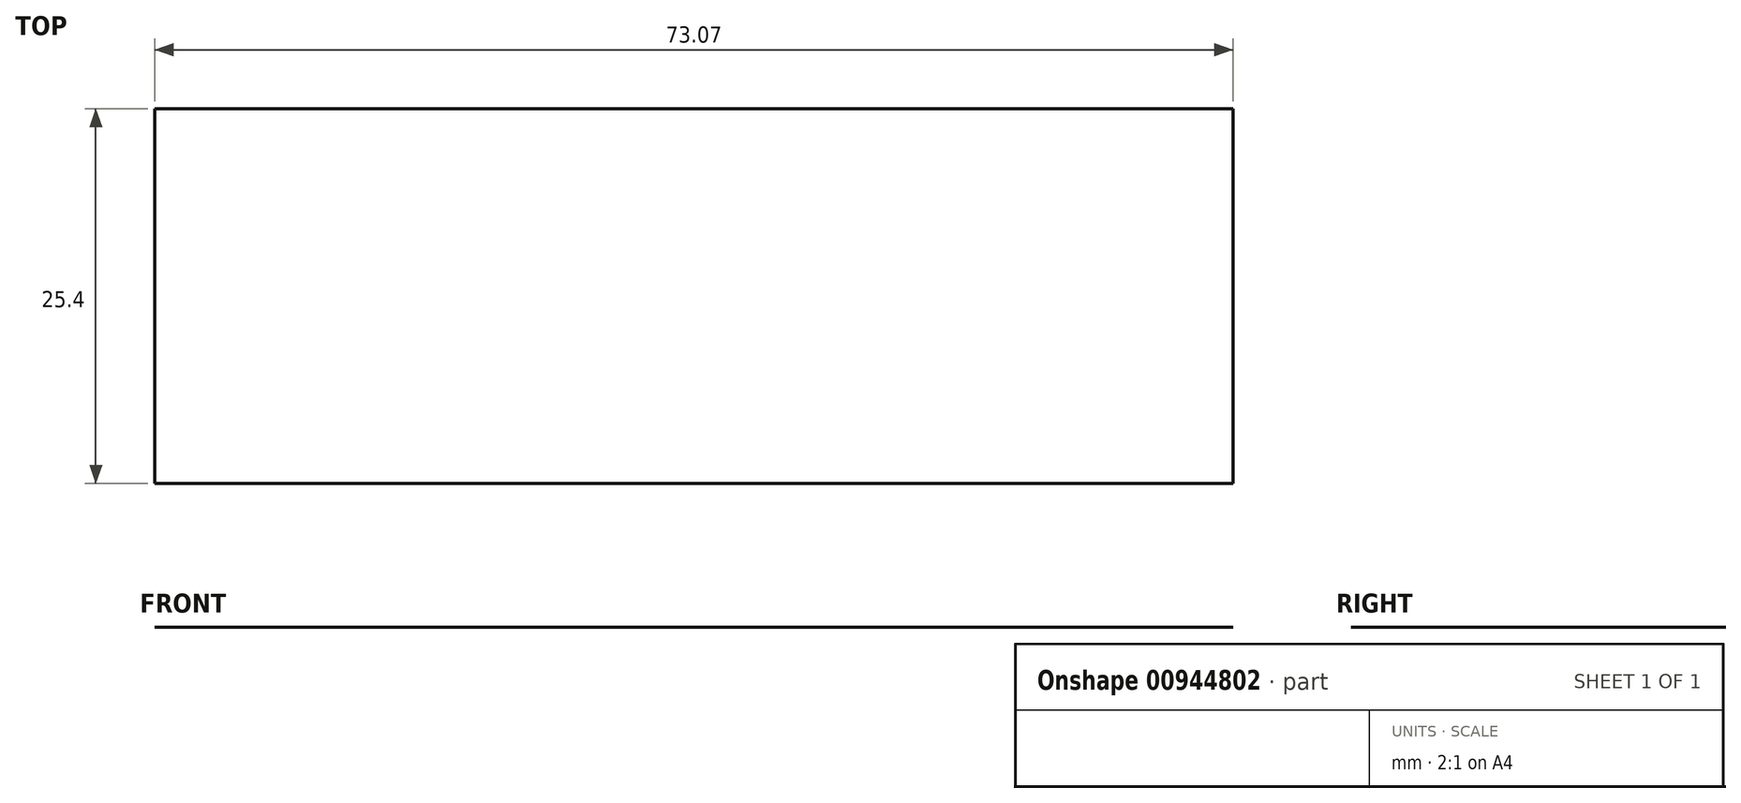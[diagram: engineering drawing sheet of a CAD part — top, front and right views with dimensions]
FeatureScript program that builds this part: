
annotation { "Feature Type Name" : "Feature", "Feature Type Description" : "" }
export const myFeature = defineFeature(function(context is Context, id is Id, definition is map)
    precondition{}
    {
        {
            var Q0;
            Q0=qCreatedBy(makeId("Front.planeOp"),FACE);
            var sketch = newSketch(context, id + "F0", { "sketchPlane" : qUnion([Q0])});
            skLineSegment(sketch, "E0.bottom", {"start": v(-34.39, 25.96) * mm, "end": v(38.68, 25.96) * mm});
            skLineSegment(sketch, "E0.top", {"start": v(-34.39, -37.55) * mm, "end": v(38.68, -37.55) * mm});
            skLineSegment(sketch, "E0.left", {"start": v(-34.39, 25.96) * mm, "end": v(-34.39, -37.55) * mm});
            skLineSegment(sketch, "E0.right", {"start": v(38.68, 25.96) * mm, "end": v(38.68, -37.55) * mm});
            skSolve(sketch);
        }
        {
            var Q0;
            Q0=sQuery(id+"F0.wireOp",EDGE,"E0.bottom");
            extrude(context, id + "F1", {"bodyType" : ToolBodyType.SURFACE, "surfaceEntities" : qUnion([Q0]), "depth" : 25.4 * mm, "offsetDistance" : 25.4 * mm});
        }
    });
